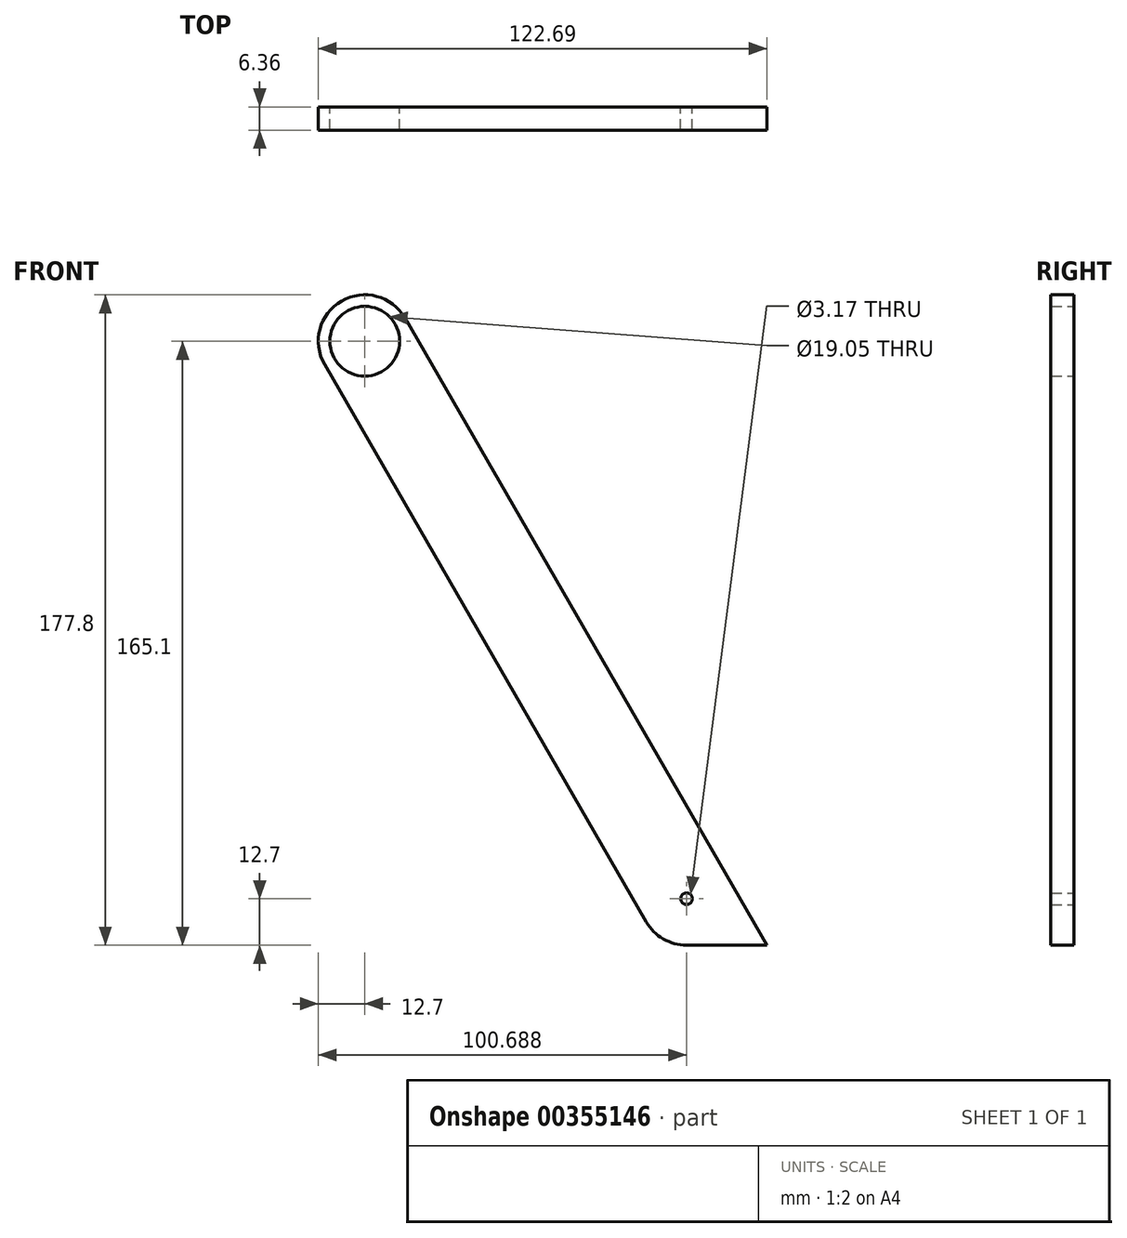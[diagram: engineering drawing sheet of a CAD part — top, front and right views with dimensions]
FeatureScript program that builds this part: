
annotation { "Feature Type Name" : "Feature", "Feature Type Description" : "" }
export const myFeature = defineFeature(function(context is Context, id is Id, definition is map)
    precondition{}
    {
        {
            var Q0;
            Q0=qCreatedBy(makeId("Front.planeOp"),FACE);
            var sketch = newSketch(context, id + "F0", { "sketchPlane" : qUnion([Q0])});
            skLineSegment(sketch, "E0", {"start": v(87.99, -152.4) * mm, "end": v(-263.96, -152.4) * mm});
            skLineSegment(sketch, "E1", {"start": v(-263.96, -152.4) * mm, "end": v(0, 0) * mm});
            skLineSegment(sketch, "E2", {"start": v(0, 0) * mm, "end": v(87.99, -152.4) * mm});
            skLineSegment(sketch, "E3", {"start": v(0, 0) * mm, "end": v(152.4, 87.99) * mm, "construction": true});
            skLineSegment(sketch, "E4", {"start": v(152.4, 87.99) * mm, "end": v(87.99, -152.4) * mm, "construction": true});
            skCircle(sketch, "E5", {"center": v(0, 0) * mm, "radius": 9.53 * mm});
            skCircle(sketch, "E6", {"center": v(0, 0) * mm, "radius": 12.7 * mm});
            skCircle(sketch, "E7", {"center": v(-263.96, -152.4) * mm, "radius": 12.7 * mm});
            skCircle(sketch, "E8", {"center": v(87.99, -152.4) * mm, "radius": 12.7 * mm});
            skLineSegment(sketch, "E9", {"start": v(-6.35, 11) * mm, "end": v(-270.31, -141.4) * mm});
            skLineSegment(sketch, "E10", {"start": v(-263.96, -165.1) * mm, "end": v(87.99, -165.1) * mm});
            skLineSegment(sketch, "E11", {"start": v(98.99, -146.05) * mm, "end": v(11, 6.35) * mm});
            skLineSegment(sketch, "E12", {"start": v(76.99, -158.75) * mm, "end": v(-11, -6.35) * mm});
            skLineSegment(sketch, "E13", {"start": v(-257.61, -163.4) * mm, "end": v(6.35, -11) * mm});
            skLineSegment(sketch, "E14", {"start": v(87.99, -139.7) * mm, "end": v(-263.96, -139.7) * mm});
            skLineSegment(sketch, "E15", {"start": v(87.99, -165.1) * mm, "end": v(109.99, -165.1) * mm});
            skLineSegment(sketch, "E16", {"start": v(98.99, -146.05) * mm, "end": v(109.99, -165.1) * mm});
            skCircle(sketch, "E17", {"center": v(87.99, -152.4) * mm, "radius": 1.59 * mm});
            skCircle(sketch, "E18", {"center": v(-263.96, -152.4) * mm, "radius": 1.59 * mm});
            skLineSegment(sketch, "E19", {"start": v(-270.31, -141.4) * mm, "end": v(-311.36, -165.1) * mm});
            skLineSegment(sketch, "E20", {"start": v(-263.96, -165.1) * mm, "end": v(-311.36, -165.1) * mm});
            skSolve(sketch);
        }
        {
            var Q0;
            {var subQ0=sQuery(id+"F0.wireOp",EDGE,"E15");Q0=makeQuery(id+"F0.imprint","IMPRINT",FACE,{"disambiguationData":[TD([[makeQuery(id+"F0.imprint","IMPRINT",EDGE,{"derivedFrom":subQ0}),1.0]])]});}
            var Q1;
            {var subQ4=sQuery(id+"F0.wireOp",EDGE,"E17");var subQ7=sQuery(id+"F0.wireOp",EDGE,"E0");var subQ8=makeQuery(id+"F0.imprint","INTERSECT",VERTEX,{"derivedFrom":[subQ7,subQ4]});Q1=makeQuery(id+"F0.imprint","IMPRINT",FACE,{"disambiguationData":[TD([[makeQuery(id+"F0.imprint","IMPRINT",EDGE,{"disambiguationData":[TD([[subQ8,-1.0]])],"derivedFrom":subQ7}),1.0]])]});}
            var Q2;
            {var subQ0=sQuery(id+"F0.wireOp",EDGE,"E17");var subQ1=sQuery(id+"F0.wireOp",EDGE,"E0");var subQ2=makeQuery(id+"F0.imprint","INTERSECT",VERTEX,{"derivedFrom":[subQ1,subQ0]});Q2=makeQuery(id+"F0.imprint","IMPRINT",FACE,{"disambiguationData":[TD([[makeQuery(id+"F0.imprint","IMPRINT",EDGE,{"disambiguationData":[TD([[subQ2,-1.0]])],"derivedFrom":subQ1}),-1.0]])]});}
            var Q3;
            {var subQ0=sQuery(id+"F0.wireOp",EDGE,"E8");var subQ1=sQuery(id+"F0.wireOp",EDGE,"E0");var subQ2=makeQuery(id+"F0.imprint","INTERSECT",VERTEX,{"derivedFrom":[subQ1,subQ0]});Q3=makeQuery(id+"F0.imprint","IMPRINT",FACE,{"disambiguationData":[TD([[makeQuery(id+"F0.imprint","IMPRINT",EDGE,{"disambiguationData":[TD([[subQ2,-1.0]])],"derivedFrom":subQ1}),-1.0]])]});}
            var Q4;
            {var subQ0=sQuery(id+"F0.wireOp",EDGE,"E14");var subQ1=sQuery(id+"F0.wireOp",EDGE,"E2");var subQ2=makeQuery(id+"F0.imprint","INTERSECT",VERTEX,{"derivedFrom":[subQ1,subQ0]});Q4=makeQuery(id+"F0.imprint","IMPRINT",FACE,{"disambiguationData":[TD([[makeQuery(id+"F0.imprint","IMPRINT",EDGE,{"disambiguationData":[TD([[subQ2,-1.0]])],"derivedFrom":subQ1}),1.0]])]});}
            var Q5;
            {var subQ0=sQuery(id+"F0.wireOp",EDGE,"E11");Q5=makeQuery(id+"F0.imprint","IMPRINT",FACE,{"disambiguationData":[TD([[makeQuery(id+"F0.imprint","IMPRINT",EDGE,{"derivedFrom":subQ0}),1.0]])]});}
            var Q6;
            {var subQ3=sQuery(id+"F0.wireOp",EDGE,"E14");var subQ5=sQuery(id+"F0.wireOp",EDGE,"E12");var subQ6=makeQuery(id+"F0.imprint","INTERSECT",VERTEX,{"derivedFrom":[subQ5,subQ3]});Q6=makeQuery(id+"F0.imprint","IMPRINT",FACE,{"disambiguationData":[TD([[makeQuery(id+"F0.imprint","IMPRINT",EDGE,{"disambiguationData":[TD([[subQ6,-1.0]])],"derivedFrom":subQ5}),-1.0]])]});}
            var Q7;
            {var subQ0=sQuery(id+"F0.wireOp",EDGE,"E8");var subQ1=sQuery(id+"F0.wireOp",EDGE,"E0");var subQ2=makeQuery(id+"F0.imprint","INTERSECT",VERTEX,{"derivedFrom":[subQ1,subQ0]});Q7=makeQuery(id+"F0.imprint","IMPRINT",FACE,{"disambiguationData":[TD([[makeQuery(id+"F0.imprint","IMPRINT",EDGE,{"disambiguationData":[TD([[subQ2,-1.0]])],"derivedFrom":subQ1}),1.0]])]});}
            var Q8;
            {var subQ0=sQuery(id+"F0.wireOp",EDGE,"E5");var subQ1=sQuery(id+"F0.wireOp",EDGE,"E1");var subQ2=makeQuery(id+"F0.imprint","INTERSECT",VERTEX,{"derivedFrom":[subQ1,subQ0]});Q8=makeQuery(id+"F0.imprint","IMPRINT",FACE,{"disambiguationData":[TD([[makeQuery(id+"F0.imprint","IMPRINT",EDGE,{"disambiguationData":[TD([[subQ2,1.0]])],"derivedFrom":subQ0}),-1.0]])]});}
            var Q9;
            {var subQ1=sQuery(id+"F0.wireOp",EDGE,"E1");var subQ3=sQuery(id+"F0.wireOp",EDGE,"E5");var subQ4=makeQuery(id+"F0.imprint","INTERSECT",VERTEX,{"derivedFrom":[subQ1,subQ3]});Q9=makeQuery(id+"F0.imprint","IMPRINT",FACE,{"disambiguationData":[TD([[makeQuery(id+"F0.imprint","IMPRINT",EDGE,{"disambiguationData":[TD([[subQ4,-1.0]])],"derivedFrom":subQ3}),-1.0]])]});}
            var Q10;
            {var subQ0=sQuery(id+"F0.wireOp",EDGE,"E12");var subQ3=sQuery(id+"F0.wireOp",EDGE,"E13");var subQ5=makeQuery(id+"F0.imprint","INTERSECT",VERTEX,{"derivedFrom":[subQ0,subQ3]});Q10=makeQuery(id+"F0.imprint","IMPRINT",FACE,{"disambiguationData":[TD([[makeQuery(id+"F0.imprint","IMPRINT",EDGE,{"disambiguationData":[TD([[subQ5,-1.0]])],"derivedFrom":subQ0}),-1.0]])]});}
            extrude(context, id + "F1", {"entities" : qUnion([Q0, Q1, Q2, Q3, Q4, Q5, Q6, Q7, Q8, Q9, Q10]), "endBound" : BoundingType.SYMMETRIC, "depth" : 6.35 * mm});
        }
    });
